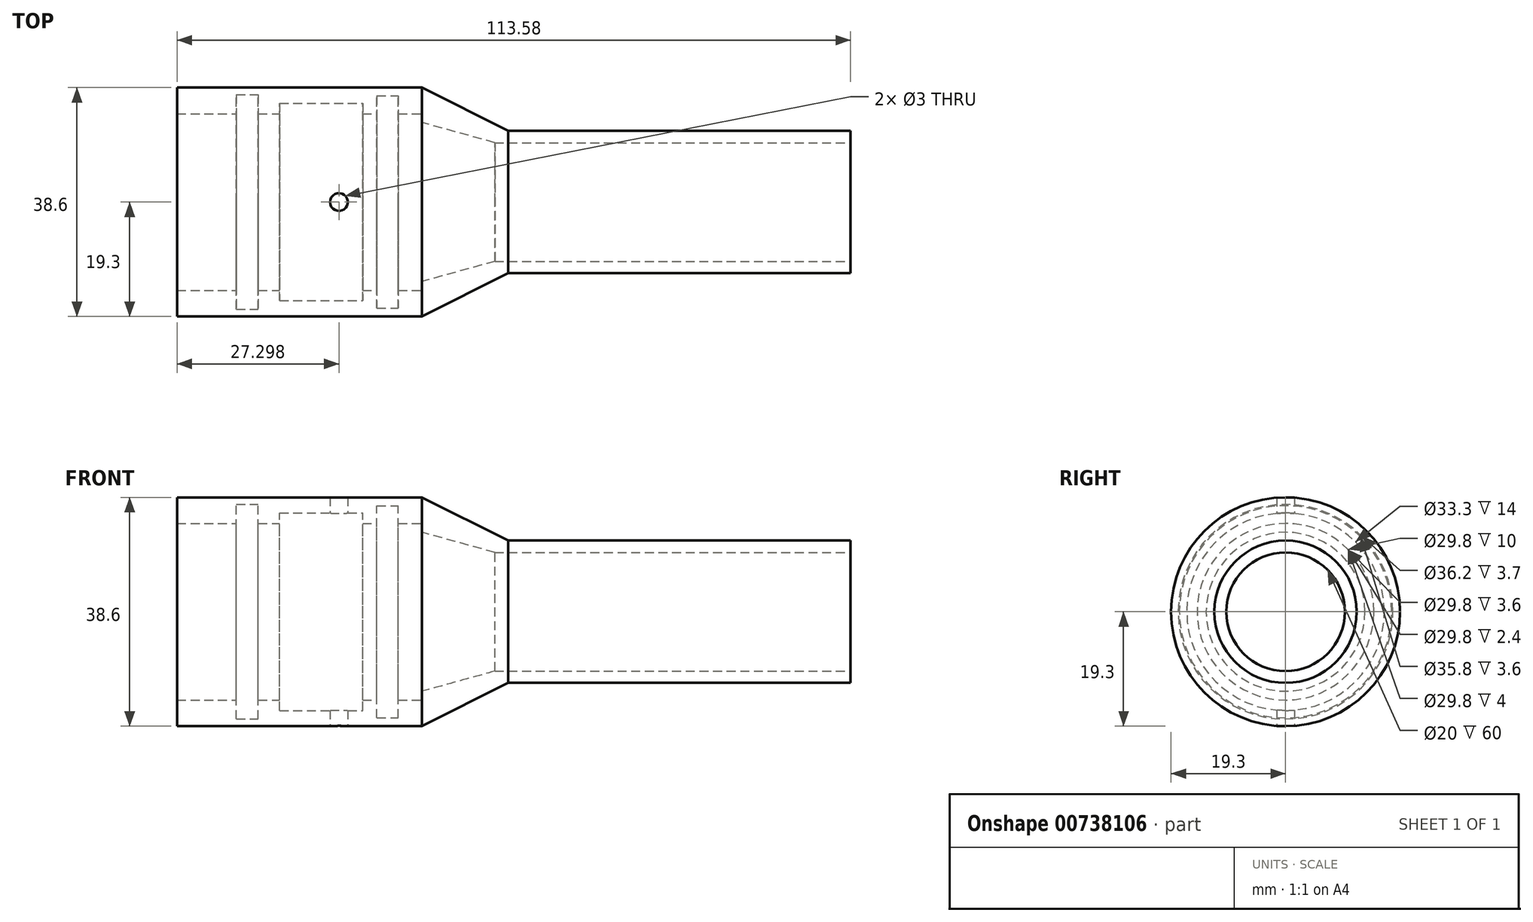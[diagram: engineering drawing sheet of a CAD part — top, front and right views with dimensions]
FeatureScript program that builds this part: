
annotation { "Feature Type Name" : "Feature", "Feature Type Description" : "" }
export const myFeature = defineFeature(function(context is Context, id is Id, definition is map)
    precondition{}
    {
        {
            var Q0;
            Q0=qCreatedBy(makeId("Front.planeOp"),FACE);
            var sketch = newSketch(context, id + "F0", { "sketchPlane" : qUnion([Q0])});
            skLineSegment(sketch, "E0", {"start": v(57.68, 0) * mm, "end": v(-89.2, 0) * mm, "construction": true});
            skLineSegment(sketch, "E1", {"start": v(-78.08, 19.3) * mm, "end": v(-78.08, -21.98) * mm, "construction": true});
            skLineSegment(sketch, "E2", {"start": v(-78.08, 19.3) * mm, "end": v(-36.78, 19.3) * mm});
            skLineSegment(sketch, "E3", {"start": v(-78.08, 14.9) * mm, "end": v(-78.08, 19.3) * mm});
            skLineSegment(sketch, "E4", {"start": v(-36.78, 14.9) * mm, "end": v(-40.78, 14.9) * mm});
            skLineSegment(sketch, "E5", {"start": v(-40.78, 14.9) * mm, "end": v(-40.78, 17.9) * mm});
            skLineSegment(sketch, "E6", {"start": v(-44.38, 17.9) * mm, "end": v(-44.38, 14.9) * mm});
            skLineSegment(sketch, "E7", {"start": v(-44.38, 14.9) * mm, "end": v(-46.78, 14.9) * mm});
            skLineSegment(sketch, "E8", {"start": v(-64.38, 14.9) * mm, "end": v(-64.38, 18.1) * mm});
            skLineSegment(sketch, "E9", {"start": v(-64.38, 18.1) * mm, "end": v(-68.08, 18.1) * mm});
            skLineSegment(sketch, "E10", {"start": v(-68.08, 18.1) * mm, "end": v(-68.08, 14.9) * mm});
            skLineSegment(sketch, "E11", {"start": v(-68.08, 14.9) * mm, "end": v(-78.08, 14.9) * mm});
            skLineSegment(sketch, "E12", {"start": v(-22.25, 12) * mm, "end": v(35.5, 12) * mm});
            skLineSegment(sketch, "E13", {"start": v(35.5, 10) * mm, "end": v(-24.5, 10) * mm});
            skLineSegment(sketch, "E14", {"start": v(35.5, 12) * mm, "end": v(35.5, 10) * mm});
            skLineSegment(sketch, "E15", {"start": v(-36.78, 19.3) * mm, "end": v(-22.25, 12) * mm});
            skLineSegment(sketch, "E16", {"start": v(-78.08, 14.9) * mm, "end": v(-78.08, 0) * mm});
            skLineSegment(sketch, "E17", {"start": v(-36.78, 14.9) * mm, "end": v(-36.78, 13.4) * mm});
            skLineSegment(sketch, "E18", {"start": v(-36.78, 13.4) * mm, "end": v(-24.5, 10) * mm});
            skLineSegment(sketch, "E19", {"start": v(-60.78, 16.65) * mm, "end": v(-46.78, 16.65) * mm});
            skLineSegment(sketch, "E20", {"start": v(-60.78, 16.65) * mm, "end": v(-60.78, 14.9) * mm});
            skLineSegment(sketch, "E21", {"start": v(-46.78, 16.65) * mm, "end": v(-46.78, 14.9) * mm});
            skLineSegment(sketch, "E22.trimOffspring", {"start": v(-60.78, 14.9) * mm, "end": v(-64.38, 14.9) * mm});
            skLineSegment(sketch, "E23", {"start": v(-44.38, 17.9) * mm, "end": v(-40.78, 17.9) * mm});
            skPoint(sketch, "E24.orphan", {"position": v(-44.38, 18.1) * mm});
            skSolve(sketch);
        }
        {
            var Q0;
            Q0=makeQuery(id+"F0.imprint","IMPRINT",FACE,{"disambiguationData":[TD([[makeQuery(id+"F0.imprint","IMPRINT",EDGE,{"derivedFrom":sQuery(id+"F0.wireOp",EDGE,"E2")}),-1.0]])]});
            var Q1;
            Q1=sQuery(id+"F0.wireOp",EDGE,"E0");
            revolve(context, id + "F1", {"surfaceOperationType" : NewSurfaceOperationType.NEW, "entities" : qUnion([Q0]), "axis" : qUnion([Q1]), "revolveType" : RevolveType.FULL});
        }
        {
            var Q0;
            Q0=qCreatedBy(makeId("Top.planeOp"),FACE);
            var sketch = newSketch(context, id + "F2", { "sketchPlane" : qUnion([Q0])});
            skCircle(sketch, "E25", {"center": v(-50.78, 0) * mm, "radius": 1.5 * mm});
            skSolve(sketch);
        }
        {
            var Q0;
            Q0=makeQuery(id+"F2.imprint","IMPRINT",FACE,{"disambiguationData":[TD([[makeQuery(id+"F2.imprint","IMPRINT",EDGE,{"derivedFrom":sQuery(id+"F2.wireOp",EDGE,"E25")}),1.0]])]});
            extrude(context, id + "F3", {"entities" : qUnion([Q0]), "operationType" : NewBodyOperationType.REMOVE, "endBound" : BoundingType.SYMMETRIC, "depth" : 50 * mm, "offsetDistance" : 25 * mm});
        }
    });
